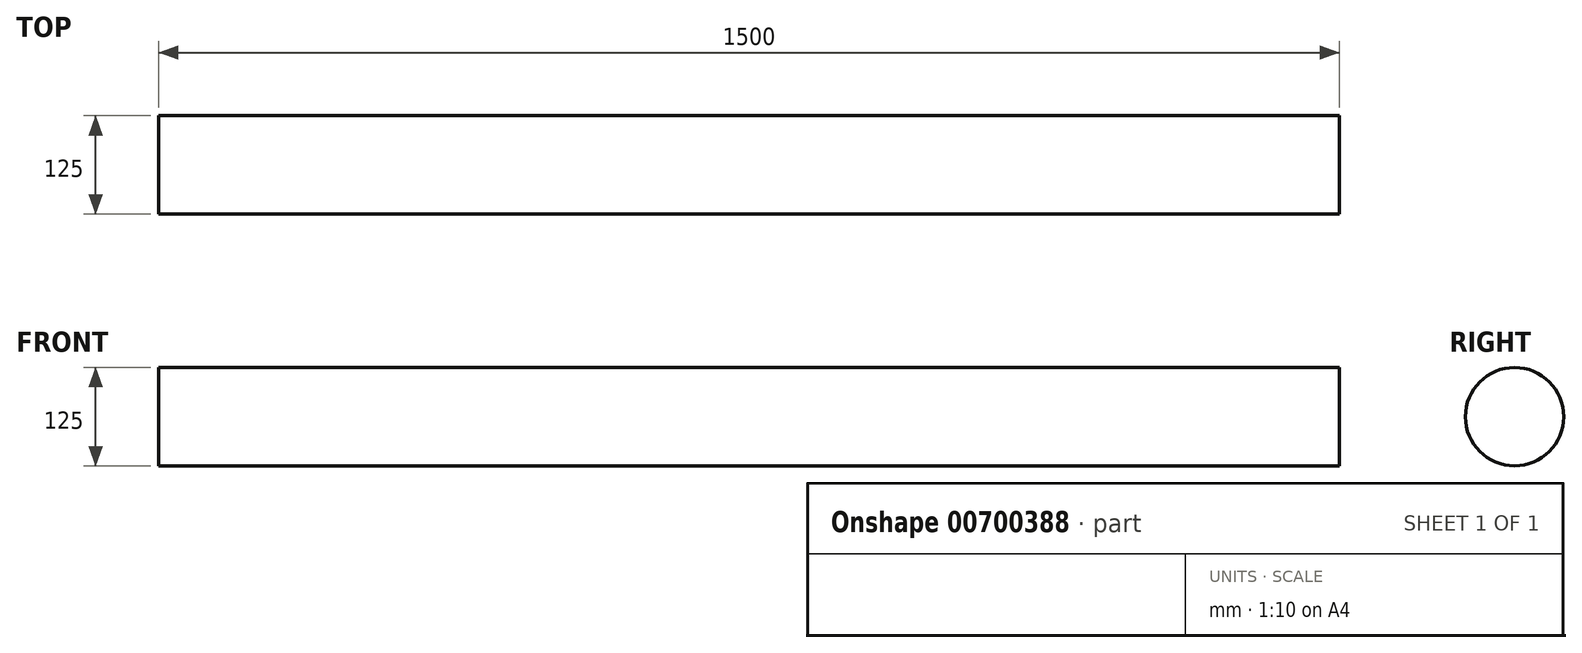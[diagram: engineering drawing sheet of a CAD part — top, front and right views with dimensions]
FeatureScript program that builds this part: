
annotation { "Feature Type Name" : "Feature", "Feature Type Description" : "" }
export const myFeature = defineFeature(function(context is Context, id is Id, definition is map)
    precondition{}
    {
        {
            var Q0;
            Q0=qCreatedBy(makeId("Right.planeOp"),FACE);
            var sketch = newSketch(context, id + "F0", { "sketchPlane" : qUnion([Q0])});
            skCircle(sketch, "E0", {"center": v(0, 0) * mm, "radius": 62.5 * mm});
            skSolve(sketch);
        }
        {
            var Q0;
            Q0=makeQuery(id+"F0.imprint","IMPRINT",FACE,{"disambiguationData":[TD([[makeQuery(id+"F0.imprint","IMPRINT",EDGE,{"derivedFrom":sQuery(id+"F0.wireOp",EDGE,"E0")}),1.0]])]});
            extrude(context, id + "F1", {"entities" : qUnion([Q0]), "depth" : 1500 * mm, "offsetDistance" : 25 * mm});
        }
    });
